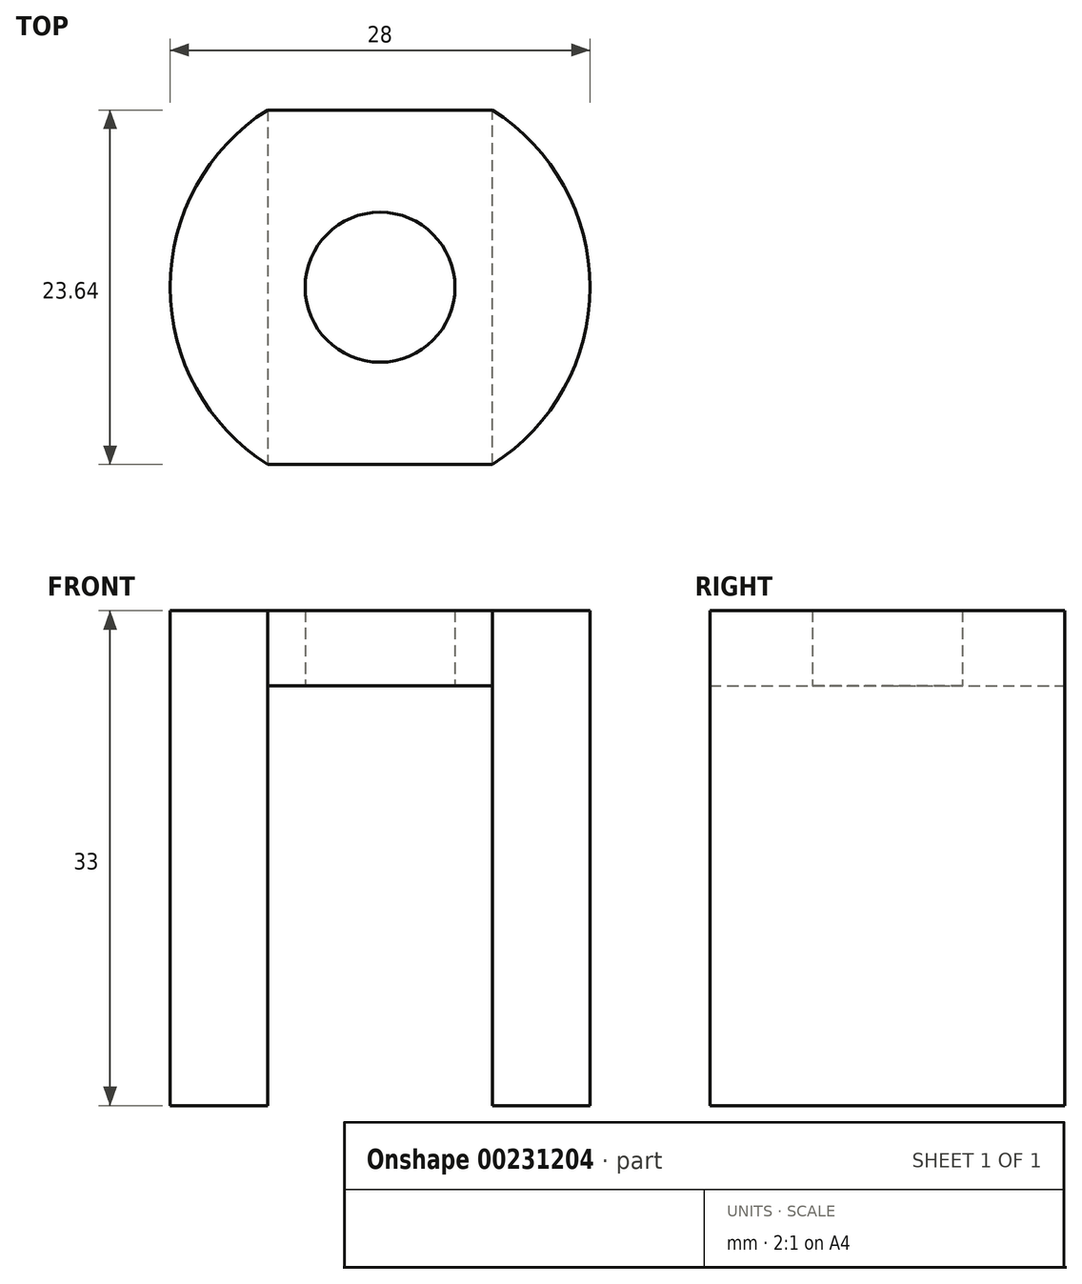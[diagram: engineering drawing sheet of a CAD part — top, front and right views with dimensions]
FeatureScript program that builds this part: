
annotation { "Feature Type Name" : "Feature", "Feature Type Description" : "" }
export const myFeature = defineFeature(function(context is Context, id is Id, definition is map)
    precondition{}
    {
        {
            var Q0;
            Q0=qCreatedBy(makeId("Top.planeOp"),FACE);
            var sketch = newSketch(context, id + "F0", { "sketchPlane" : qUnion([Q0])});
            skCircle(sketch, "E0", {"center": v(0, 0) * mm, "radius": 14 * mm});
            skCircle(sketch, "E1", {"center": v(0, 0) * mm, "radius": 5 * mm});
            skLineSegment(sketch, "E2", {"start": v(0, 0) * mm, "end": v(-7.5, 0) * mm});
            skLineSegment(sketch, "E3", {"start": v(0, 0) * mm, "end": v(7.5, 0) * mm});
            skLineSegment(sketch, "E4", {"start": v(7.5, 0) * mm, "end": v(7.5, 11.82) * mm});
            skLineSegment(sketch, "E5", {"start": v(7.5, 0) * mm, "end": v(7.5, -11.82) * mm});
            skLineSegment(sketch, "E6", {"start": v(-7.5, 0) * mm, "end": v(-7.5, 11.82) * mm});
            skLineSegment(sketch, "E7", {"start": v(-7.5, 0) * mm, "end": v(-7.5, -11.82) * mm});
            skLineSegment(sketch, "E8", {"start": v(-7.5, -11.82) * mm, "end": v(7.5, -11.82) * mm});
            skLineSegment(sketch, "E9", {"start": v(7.5, 11.82) * mm, "end": v(-7.5, 11.82) * mm});
            skSolve(sketch);
        }
        {
            var Q0;
            {var subQ0=sQuery(id+"F0.wireOp",EDGE,"E6");Q0=makeQuery(id+"F0.imprint","IMPRINT",FACE,{"disambiguationData":[TD([[makeQuery(id+"F0.imprint","IMPRINT",EDGE,{"derivedFrom":subQ0}),1.0]])]});}
            var Q1;
            {var subQ0=sQuery(id+"F0.wireOp",EDGE,"E5");Q1=makeQuery(id+"F0.imprint","IMPRINT",FACE,{"disambiguationData":[TD([[makeQuery(id+"F0.imprint","IMPRINT",EDGE,{"derivedFrom":subQ0}),-1.0]])]});}
            var Q2;
            {var subQ0=sQuery(id+"F0.wireOp",EDGE,"E4");Q2=makeQuery(id+"F0.imprint","IMPRINT",FACE,{"disambiguationData":[TD([[makeQuery(id+"F0.imprint","IMPRINT",EDGE,{"derivedFrom":subQ0}),1.0]])]});}
            var Q3;
            {var subQ0=sQuery(id+"F0.wireOp",EDGE,"E4");Q3=makeQuery(id+"F0.imprint","IMPRINT",FACE,{"disambiguationData":[TD([[makeQuery(id+"F0.imprint","IMPRINT",EDGE,{"derivedFrom":subQ0}),-1.0]])]});}
            extrude(context, id + "F1", {"entities" : qUnion([Q0, Q1, Q2, Q3]), "depth" : 5 * mm});
        }
        {
            var Q0;
            {var subQ0=sQuery(id+"F0.wireOp",EDGE,"E6");Q0=makeQuery(id+"F0.imprint","IMPRINT",FACE,{"disambiguationData":[TD([[makeQuery(id+"F0.imprint","IMPRINT",EDGE,{"derivedFrom":subQ0}),1.0]])]});}
            var Q1;
            {var subQ0=sQuery(id+"F0.wireOp",EDGE,"E4");Q1=makeQuery(id+"F0.imprint","IMPRINT",FACE,{"disambiguationData":[TD([[makeQuery(id+"F0.imprint","IMPRINT",EDGE,{"derivedFrom":subQ0}),-1.0]])]});}
            extrude(context, id + "F2", {"entities" : qUnion([Q0, Q1]), "operationType" : NewBodyOperationType.ADD, "oppositeDirection" : true, "depth" : 28 * mm});
        }
    });
